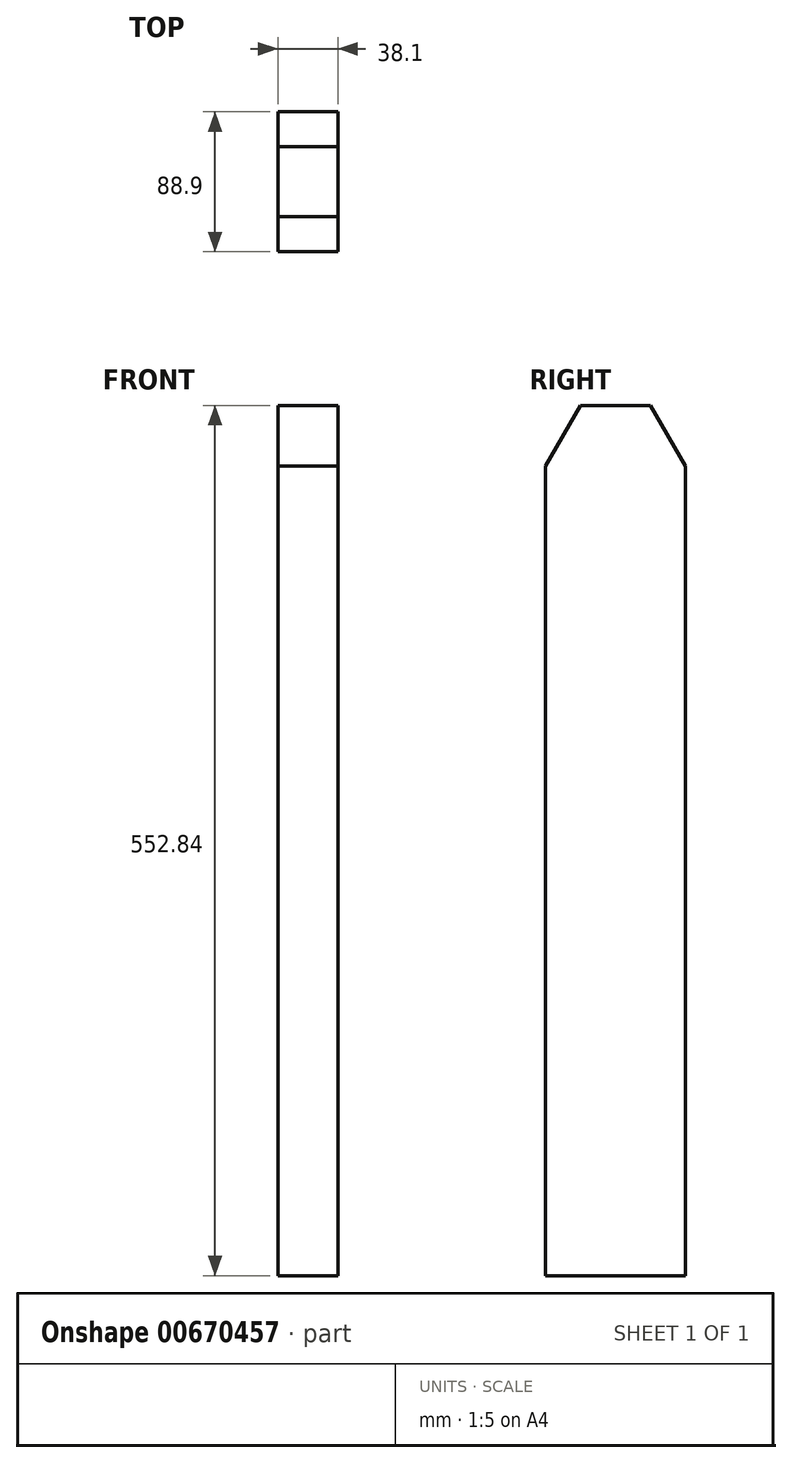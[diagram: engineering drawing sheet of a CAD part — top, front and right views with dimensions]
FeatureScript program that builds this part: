
annotation { "Feature Type Name" : "Feature", "Feature Type Description" : "" }
export const myFeature = defineFeature(function(context is Context, id is Id, definition is map)
    precondition{}
    {
        {
            var Q0;
            Q0=qCreatedBy(makeId("Right.planeOp"),FACE);
            var sketch = newSketch(context, id + "F0", { "sketchPlane" : qUnion([Q0])});
            skLineSegment(sketch, "E0.bottom", {"start": v(0, 0) * mm, "end": v(88.9, 0) * mm});
            skLineSegment(sketch, "E0.top", {"start": v(44.45, 558.8) * mm, "end": v(44.45, 558.8) * mm});
            skLineSegment(sketch, "E0.left", {"start": v(0, 0) * mm, "end": v(0, 514.35) * mm});
            skLineSegment(sketch, "E0.right", {"start": v(88.9, 0) * mm, "end": v(88.9, 514.35) * mm});
            skPoint(sketch, "E1.visualSharp", {"position": v(0, 558.8) * mm});
            skArc(sketch, "E1.filletArc", {"start": v(44.45, 558.8) * mm, "mid": v(13.02, 545.78) * mm, "end": v(0, 514.35) * mm, "construction": true});
            skPoint(sketch, "E2.visualSharp", {"position": v(88.9, 558.8) * mm});
            skArc(sketch, "E2.filletArc", {"start": v(88.9, 514.35) * mm, "mid": v(75.88, 545.78) * mm, "end": v(44.45, 558.8) * mm});
            skLineSegment(sketch, "E3", {"start": v(0, 514.35) * mm, "end": v(22.23, 552.84) * mm});
            skLineSegment(sketch, "E4", {"start": v(22.23, 552.84) * mm, "end": v(66.68, 552.84) * mm});
            skLineSegment(sketch, "E5", {"start": v(66.68, 552.84) * mm, "end": v(88.9, 514.35) * mm});
            skSolve(sketch);
        }
        {
            var Q0;
            Q0=makeQuery(id+"F0.imprint","IMPRINT",FACE,{"disambiguationData":[TD([[makeQuery(id+"F0.imprint","IMPRINT",EDGE,{"derivedFrom":sQuery(id+"F0.wireOp",EDGE,"E0.bottom")}),1.0]])]});
            extrude(context, id + "F1", {"entities" : qUnion([Q0]), "depth" : 38.1 * mm, "offsetDistance" : 25.4 * mm});
        }
    });
